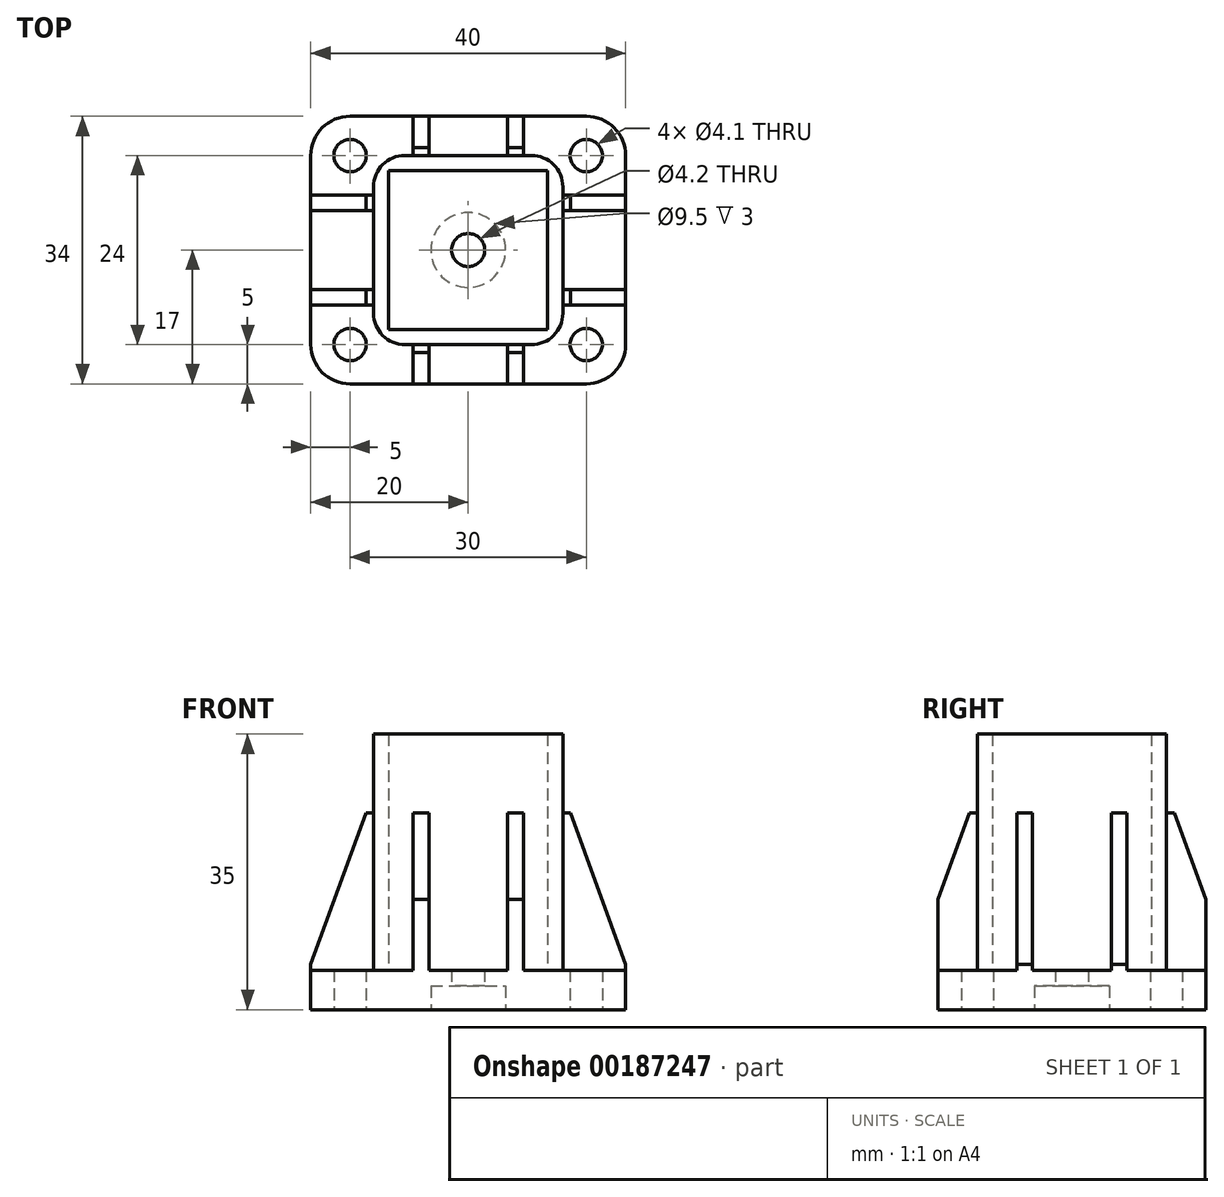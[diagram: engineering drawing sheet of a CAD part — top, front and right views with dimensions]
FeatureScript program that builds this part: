
annotation { "Feature Type Name" : "Feature", "Feature Type Description" : "" }
export const myFeature = defineFeature(function(context is Context, id is Id, definition is map)
    precondition{}
    {
        {
            var Q0;
            Q0=qCreatedBy(makeId("Top.planeOp"),FACE);
            var sketch = newSketch(context, id + "F0", { "sketchPlane" : qUnion([Q0])});
            skLineSegment(sketch, "E0.bottom", {"start": v(20, -17) * mm, "end": v(-20, -17) * mm});
            skLineSegment(sketch, "E0.top", {"start": v(20, 17) * mm, "end": v(-20, 17) * mm});
            skLineSegment(sketch, "E0.left", {"start": v(20, -17) * mm, "end": v(20, 17) * mm});
            skLineSegment(sketch, "E0.right", {"start": v(-20, -17) * mm, "end": v(-20, 17) * mm});
            skPoint(sketch, "E0.middle", {"position": v(0, 0) * mm});
            skCircle(sketch, "E1", {"center": v(0, 0) * mm, "radius": 2.1 * mm});
            skLineSegment(sketch, "E2", {"start": v(0, 0) * mm, "end": v(15, 0) * mm, "construction": true});
            skLineSegment(sketch, "E3", {"start": v(15, 0) * mm, "end": v(15, 12) * mm, "construction": true});
            skCircle(sketch, "E4", {"center": v(15, 12) * mm, "radius": 2.05 * mm});
            skLineSegment(sketch, "E5", {"start": v(0, 0) * mm, "end": v(0, 15.27) * mm, "construction": true});
            skLineSegment(sketch, "E6", {"start": v(0, 0) * mm, "end": v(0, -14.9) * mm, "construction": true});
            skCircle(sketch, "E7.MirrorC", {"center": v(15, -12) * mm, "radius": 2.05 * mm});
            skCircle(sketch, "E8.MirrorC", {"center": v(-15, 12) * mm, "radius": 2.05 * mm});
            skCircle(sketch, "E9.MirrorC", {"center": v(-15, -12) * mm, "radius": 2.05 * mm});
            skSolve(sketch);
        }
        {
            var Q0;
            Q0=makeQuery(id+"F0.imprint","IMPRINT",FACE,{"disambiguationData":[TD([[makeQuery(id+"F0.imprint","IMPRINT",EDGE,{"derivedFrom":sQuery(id+"F0.wireOp",EDGE,"E0.bottom")}),-1.0]])]});
            extrude(context, id + "F1", {"entities" : qUnion([Q0]), "depth" : 5 * mm});
        }
        {
            var Q0;
            Q0=makeQuery(id+"F1.opExtrude","CAP_FACE",FACE,{"disambiguationData":[OSD([sQuery(id+"F0.wireOp",EDGE,"E0.bottom"),sQuery(id+"F0.wireOp",EDGE,"E0.top"),sQuery(id+"F0.wireOp",EDGE,"E0.left"),sQuery(id+"F0.wireOp",EDGE,"E0.right"),sQuery(id+"F0.wireOp",EDGE,"E1"),sQuery(id+"F0.wireOp",EDGE,"E4"),sQuery(id+"F0.wireOp",EDGE,"E7.MirrorC"),sQuery(id+"F0.wireOp",EDGE,"E8.MirrorC"),sQuery(id+"F0.wireOp",EDGE,"E9.MirrorC")])],"isStart":true});
            var sketch = newSketch(context, id + "F2", { "sketchPlane" : qUnion([Q0])});
            skCircle(sketch, "E10", {"center": v(0, 0) * mm, "radius": 4.75 * mm});
            skSolve(sketch);
        }
        {
            var Q0;
            Q0=makeQuery(id+"F2.imprint","IMPRINT",FACE,{"disambiguationData":[TD([[makeQuery(id+"F2.imprint","IMPRINT",EDGE,{"derivedFrom":sQuery(id+"F2.wireOp",EDGE,"E10")}),1.0]])]});
            extrude(context, id + "F3", {"entities" : qUnion([Q0]), "operationType" : NewBodyOperationType.REMOVE, "oppositeDirection" : true, "depth" : 3 * mm});
        }
        {
            var Q0;
            Q0=makeQuery(id+"F1.opExtrude","CAP_FACE",FACE,{"disambiguationData":[OSD([sQuery(id+"F0.wireOp",EDGE,"E0.bottom"),sQuery(id+"F0.wireOp",EDGE,"E0.top"),sQuery(id+"F0.wireOp",EDGE,"E0.left"),sQuery(id+"F0.wireOp",EDGE,"E0.right"),sQuery(id+"F0.wireOp",EDGE,"E1"),sQuery(id+"F0.wireOp",EDGE,"E4"),sQuery(id+"F0.wireOp",EDGE,"E7.MirrorC"),sQuery(id+"F0.wireOp",EDGE,"E8.MirrorC"),sQuery(id+"F0.wireOp",EDGE,"E9.MirrorC")])],"isStart":false});
            var sketch = newSketch(context, id + "F4", { "sketchPlane" : qUnion([Q0])});
            skLineSegment(sketch, "E11.bottom", {"start": v(10.1, -10.1) * mm, "end": v(-10.1, -10.1) * mm});
            skLineSegment(sketch, "E11.top", {"start": v(10.1, 10.1) * mm, "end": v(-10.1, 10.1) * mm});
            skLineSegment(sketch, "E11.left", {"start": v(10.1, -10.1) * mm, "end": v(10.1, 10.1) * mm});
            skLineSegment(sketch, "E11.right", {"start": v(-10.1, -10.1) * mm, "end": v(-10.1, 10.1) * mm});
            skPoint(sketch, "E11.middle", {"position": v(0, 0) * mm});
            skLineSegment(sketch, "E12.bottom", {"start": v(12.03, -12.03) * mm, "end": v(-12.03, -12.03) * mm});
            skLineSegment(sketch, "E12.top", {"start": v(12.03, 12.03) * mm, "end": v(-12.03, 12.02) * mm});
            skLineSegment(sketch, "E12.left", {"start": v(12.03, -12.03) * mm, "end": v(12.03, 12.03) * mm});
            skLineSegment(sketch, "E12.right", {"start": v(-12.03, -12.03) * mm, "end": v(-12.03, 12.02) * mm});
            skLineSegment(sketch, "E13", {"start": v(0, 0) * mm, "end": v(0, 17) * mm, "construction": true});
            skLineSegment(sketch, "E14", {"start": v(0, 0) * mm, "end": v(20, 0) * mm, "construction": true});
            skPoint(sketch, "E15.end.orphan", {"position": v(1, 17) * mm});
            skPoint(sketch, "E15.start.orphan", {"position": v(1, 12.02) * mm});
            skPoint(sketch, "E16.MirrorCS.end.orphan", {"position": v(-1, 17) * mm});
            skPoint(sketch, "E16.MirrorCS.start.orphan", {"position": v(-1, 12.02) * mm});
            skPoint(sketch, "E17.MirrorCS.end.orphan", {"position": v(1, -17) * mm});
            skPoint(sketch, "E17.MirrorCS.start.orphan", {"position": v(1, -12.02) * mm});
            skPoint(sketch, "E18.MirrorCS.end.orphan", {"position": v(-1, -17) * mm});
            skPoint(sketch, "E18.MirrorCS.start.orphan", {"position": v(-1, -12.02) * mm});
            skPoint(sketch, "E19.end.orphan", {"position": v(7, 17) * mm});
            skPoint(sketch, "E19.start.orphan", {"position": v(7, 12.02) * mm});
            skPoint(sketch, "E20.end.orphan", {"position": v(5, 17) * mm});
            skPoint(sketch, "E20.start.orphan", {"position": v(5, 12.02) * mm});
            skPoint(sketch, "E21.MirrorCS.end.orphan", {"position": v(-5, 17) * mm});
            skPoint(sketch, "E21.MirrorCS.start.orphan", {"position": v(-5, 12.02) * mm});
            skPoint(sketch, "E22.MirrorCS.end.orphan", {"position": v(-7, 17) * mm});
            skPoint(sketch, "E22.MirrorCS.start.orphan", {"position": v(-7, 12.02) * mm});
            skPoint(sketch, "E23.end.orphan", {"position": v(20, 5) * mm});
            skPoint(sketch, "E23.start.orphan", {"position": v(12.03, 5) * mm});
            skPoint(sketch, "E24.end.orphan", {"position": v(20, 7) * mm});
            skPoint(sketch, "E24.start.orphan", {"position": v(12.03, 7) * mm});
            skPoint(sketch, "E25.MirrorCS.end.orphan", {"position": v(20, -5) * mm});
            skPoint(sketch, "E25.MirrorCS.start.orphan", {"position": v(12.03, -5) * mm});
            skPoint(sketch, "E26.MirrorCS.end.orphan", {"position": v(20, -7) * mm});
            skPoint(sketch, "E26.MirrorCS.start.orphan", {"position": v(12.03, -7) * mm});
            skPoint(sketch, "E27.MirrorCS.end.orphan", {"position": v(7, -17) * mm});
            skPoint(sketch, "E27.MirrorCS.start.orphan", {"position": v(7, -12.02) * mm});
            skPoint(sketch, "E28.MirrorCS.end.orphan", {"position": v(5, -17) * mm});
            skPoint(sketch, "E28.MirrorCS.start.orphan", {"position": v(5, -12.02) * mm});
            skPoint(sketch, "E29.MirrorCS.end.orphan", {"position": v(-5, -17) * mm});
            skPoint(sketch, "E29.MirrorCS.start.orphan", {"position": v(-5, -12.02) * mm});
            skPoint(sketch, "E30.MirrorCS.end.orphan", {"position": v(-20, 5) * mm});
            skPoint(sketch, "E30.MirrorCS.start.orphan", {"position": v(-12.03, 5) * mm});
            skPoint(sketch, "E31.MirrorCS.end.orphan", {"position": v(-20, 7) * mm});
            skPoint(sketch, "E31.MirrorCS.start.orphan", {"position": v(-12.03, 7) * mm});
            skPoint(sketch, "E32.MirrorCS.end.orphan", {"position": v(-20, -7) * mm});
            skPoint(sketch, "E32.MirrorCS.start.orphan", {"position": v(-12.03, -7) * mm});
            skPoint(sketch, "E33.MirrorCS.end.orphan", {"position": v(-20, -5) * mm});
            skPoint(sketch, "E33.MirrorCS.start.orphan", {"position": v(-12.03, -5) * mm});
            skPoint(sketch, "E34.MirrorCS.end.orphan", {"position": v(-7, -17) * mm});
            skPoint(sketch, "E34.MirrorCS.start.orphan", {"position": v(-7, -12.02) * mm});
            skSolve(sketch);
        }
        {
            var Q0;
            Q0=makeQuery(id+"F4.imprint","IMPRINT",FACE,{"disambiguationData":[TD([[makeQuery(id+"F4.imprint","IMPRINT",EDGE,{"derivedFrom":sQuery(id+"F4.wireOp",EDGE,"E11.bottom")}),1.0]])]});
            extrude(context, id + "F5", {"entities" : qUnion([Q0]), "operationType" : NewBodyOperationType.ADD, "depth" : 30 * mm});
        }
        {
            var Q0;
            Q0=makeQuery(id+"F1.opExtrude","SWEPT_EDGE",EDGE,{"disambiguationData":[OSD([sQuery(id+"F0.wireOp",EDGE,"E0.top"),sQuery(id+"F0.wireOp",EDGE,"E0.left")])]});
            var Q1;
            Q1=makeQuery(id+"F1.opExtrude","SWEPT_EDGE",EDGE,{"disambiguationData":[OSD([sQuery(id+"F0.wireOp",EDGE,"E0.bottom"),sQuery(id+"F0.wireOp",EDGE,"E0.left")])]});
            var Q2;
            Q2=makeQuery(id+"F1.opExtrude","SWEPT_EDGE",EDGE,{"disambiguationData":[OSD([sQuery(id+"F0.wireOp",EDGE,"E0.bottom"),sQuery(id+"F0.wireOp",EDGE,"E0.right")])]});
            var Q3;
            Q3=makeQuery(id+"F1.opExtrude","SWEPT_EDGE",EDGE,{"disambiguationData":[OSD([sQuery(id+"F0.wireOp",EDGE,"E0.top"),sQuery(id+"F0.wireOp",EDGE,"E0.right")])]});
            fillet(context, id + "F6", {"entities" : qUnion([Q0, Q1, Q2, Q3]), "radius" : 5 * mm, "tangentPropagation" : true, "allowEdgeOverflow" : false});
        }
        {
            var Q0;
            Q0=makeQuery(id+"F5.opExtrude","SWEPT_EDGE",EDGE,{"disambiguationData":[OSD([sQuery(id+"F4.wireOp",EDGE,"E12.bottom"),sQuery(id+"F4.wireOp",EDGE,"E12.left")])]});
            var Q1;
            Q1=makeQuery(id+"F5.opExtrude","SWEPT_EDGE",EDGE,{"disambiguationData":[OSD([sQuery(id+"F4.wireOp",EDGE,"E12.top"),sQuery(id+"F4.wireOp",EDGE,"E12.left")])]});
            var Q2;
            Q2=makeQuery(id+"F5.opExtrude","SWEPT_EDGE",EDGE,{"disambiguationData":[OSD([sQuery(id+"F4.wireOp",EDGE,"E12.bottom"),sQuery(id+"F4.wireOp",EDGE,"E12.right")])]});
            var Q3;
            Q3=makeQuery(id+"F5.opExtrude","SWEPT_EDGE",EDGE,{"disambiguationData":[OSD([sQuery(id+"F4.wireOp",EDGE,"E12.top"),sQuery(id+"F4.wireOp",EDGE,"E12.right")])]});
            fillet(context, id + "F7", {"entities" : qUnion([Q0, Q1, Q2, Q3]), "radius" : 4 * mm, "tangentPropagation" : true, "allowEdgeOverflow" : false});
        }
        {
            var Q0;
            {var subQ0=sQuery(id+"F0.wireOp",EDGE,"E8.MirrorC");var subQ1=sQuery(id+"F0.wireOp",EDGE,"E7.MirrorC");var subQ2=sQuery(id+"F0.wireOp",EDGE,"E4");var subQ3=sQuery(id+"F0.wireOp",EDGE,"E0.bottom");var subQ4=sQuery(id+"F0.wireOp",EDGE,"E9.MirrorC");var subQ5=sQuery(id+"F0.wireOp",EDGE,"E0.top");var subQ6=sQuery(id+"F0.wireOp",EDGE,"E0.left");var subQ7=sQuery(id+"F0.wireOp",EDGE,"E0.right");Q0=makeQuery(id+"F5.boolean.opBoolean","SPLIT",FACE,{"disambiguationData":[TD([makeQuery(id+"F1.opExtrude","SWEPT_FACE",FACE,{"disambiguationData":[OSD([subQ3])]})])],"derivedFrom":makeQuery(id+"F1.opExtrude","CAP_FACE",FACE,{"disambiguationData":[OSD([subQ3,subQ5,subQ6,subQ7,sQuery(id+"F0.wireOp",EDGE,"E1"),subQ2,subQ1,subQ0,subQ4])],"isStart":false})});}
            var sketch = newSketch(context, id + "F8", { "sketchPlane" : qUnion([Q0])});
            skLineSegment(sketch, "E35", {"start": v(0, 0) * mm, "end": v(0, 17) * mm, "construction": true});
            skLineSegment(sketch, "E36", {"start": v(0, 0) * mm, "end": v(20, 0) * mm, "construction": true});
            skLineSegment(sketch, "E37", {"start": v(5, 12.03) * mm, "end": v(5, 17) * mm});
            skLineSegment(sketch, "E38", {"start": v(7, 12.03) * mm, "end": v(7, 17) * mm});
            skLineSegment(sketch, "E39", {"start": v(12.03, 7) * mm, "end": v(20, 7) * mm});
            skLineSegment(sketch, "E40", {"start": v(12.03, 5) * mm, "end": v(20, 5) * mm});
            skLineSegment(sketch, "E41.MirrorCS", {"start": v(-5, 12.03) * mm, "end": v(-5, 17) * mm});
            skLineSegment(sketch, "E42.MirrorCS", {"start": v(-7, 12.03) * mm, "end": v(-7, 17) * mm});
            skLineSegment(sketch, "E43.MirrorCS", {"start": v(12.03, -5) * mm, "end": v(20, -5) * mm});
            skLineSegment(sketch, "E44.MirrorCS", {"start": v(12.03, -7) * mm, "end": v(20, -7) * mm});
            skLineSegment(sketch, "E45.MirrorCS", {"start": v(-12.03, 7) * mm, "end": v(-20, 7) * mm});
            skLineSegment(sketch, "E46.MirrorCS", {"start": v(-12.03, 5) * mm, "end": v(-20, 5) * mm});
            skLineSegment(sketch, "E47.MirrorCS", {"start": v(-12.03, -5) * mm, "end": v(-20, -5) * mm});
            skLineSegment(sketch, "E48.MirrorCS", {"start": v(-12.03, -7) * mm, "end": v(-20, -7) * mm});
            skLineSegment(sketch, "E49.MirrorCS", {"start": v(7, -12.03) * mm, "end": v(7, -17) * mm});
            skLineSegment(sketch, "E50.MirrorCS", {"start": v(5, -12.03) * mm, "end": v(5, -17) * mm});
            skLineSegment(sketch, "E51.MirrorCS", {"start": v(-5, -12.03) * mm, "end": v(-5, -17) * mm});
            skLineSegment(sketch, "E52.MirrorCS", {"start": v(-7, -12.03) * mm, "end": v(-7, -17) * mm});
            skSolve(sketch);
        }
        {
            var Q0;
            {var subQ0=sQuery(id+"F8.wireOp",EDGE,"E41.MirrorCS");Q0=makeQuery(id+"F8.imprint","IMPRINT",FACE,{"disambiguationData":[TD([[makeQuery(id+"F8.imprint","IMPRINT",EDGE,{"derivedFrom":subQ0}),1.0]])]});}
            var Q1;
            {var subQ0=sQuery(id+"F8.wireOp",EDGE,"E37");Q1=makeQuery(id+"F8.imprint","IMPRINT",FACE,{"disambiguationData":[TD([[makeQuery(id+"F8.imprint","IMPRINT",EDGE,{"derivedFrom":subQ0}),-1.0]])]});}
            var Q2;
            {var subQ0=sQuery(id+"F8.wireOp",EDGE,"E39");Q2=makeQuery(id+"F8.imprint","IMPRINT",FACE,{"disambiguationData":[TD([[makeQuery(id+"F8.imprint","IMPRINT",EDGE,{"derivedFrom":subQ0}),-1.0]])]});}
            var Q3;
            {var subQ0=sQuery(id+"F8.wireOp",EDGE,"E43.MirrorCS");Q3=makeQuery(id+"F8.imprint","IMPRINT",FACE,{"disambiguationData":[TD([[makeQuery(id+"F8.imprint","IMPRINT",EDGE,{"derivedFrom":subQ0}),-1.0]])]});}
            var Q4;
            {var subQ0=sQuery(id+"F8.wireOp",EDGE,"E49.MirrorCS");Q4=makeQuery(id+"F8.imprint","IMPRINT",FACE,{"disambiguationData":[TD([[makeQuery(id+"F8.imprint","IMPRINT",EDGE,{"derivedFrom":subQ0}),-1.0]])]});}
            var Q5;
            {var subQ0=sQuery(id+"F8.wireOp",EDGE,"E51.MirrorCS");Q5=makeQuery(id+"F8.imprint","IMPRINT",FACE,{"disambiguationData":[TD([[makeQuery(id+"F8.imprint","IMPRINT",EDGE,{"derivedFrom":subQ0}),-1.0]])]});}
            var Q6;
            {var subQ0=sQuery(id+"F8.wireOp",EDGE,"E47.MirrorCS");Q6=makeQuery(id+"F8.imprint","IMPRINT",FACE,{"disambiguationData":[TD([[makeQuery(id+"F8.imprint","IMPRINT",EDGE,{"derivedFrom":subQ0}),1.0]])]});}
            var Q7;
            {var subQ0=sQuery(id+"F8.wireOp",EDGE,"E45.MirrorCS");Q7=makeQuery(id+"F8.imprint","IMPRINT",FACE,{"disambiguationData":[TD([[makeQuery(id+"F8.imprint","IMPRINT",EDGE,{"derivedFrom":subQ0}),1.0]])]});}
            extrude(context, id + "F9", {"entities" : qUnion([Q0, Q1, Q2, Q3, Q4, Q5, Q6, Q7]), "operationType" : NewBodyOperationType.ADD, "depth" : 20 * mm});
        }
        {
            var Q0;
            {var subQ0=sQuery(id+"F0.wireOp",EDGE,"E0.left");var subQ1=makeQuery(id+"F1.opExtrude","CAP_EDGE",EDGE,{"disambiguationData":[OSD([subQ0])],"isStart":false});Q0=makeQuery(id+"F9.opExtrude","CAP_EDGE",EDGE,{"disambiguationData":[OSD([subQ0]),TDD([makeQuery(id+"F8.imprint","IMPRINT",EDGE,{"disambiguationData":[TD([[makeQuery(id+"F8.imprint","INTERSECT",VERTEX,{"derivedFrom":[subQ1,sQuery(id+"F8.wireOp",EDGE,"E39")]}),1.0]])],"derivedFrom":subQ1})])],"isStart":false});}
            var Q1;
            {var subQ0=sQuery(id+"F0.wireOp",EDGE,"E0.left");var subQ1=makeQuery(id+"F1.opExtrude","CAP_EDGE",EDGE,{"disambiguationData":[OSD([subQ0])],"isStart":false});Q1=makeQuery(id+"F9.opExtrude","CAP_EDGE",EDGE,{"disambiguationData":[OSD([subQ0]),TDD([makeQuery(id+"F8.imprint","IMPRINT",EDGE,{"disambiguationData":[TD([[makeQuery(id+"F8.imprint","INTERSECT",VERTEX,{"derivedFrom":[subQ1,sQuery(id+"F8.wireOp",EDGE,"E43.MirrorCS")]}),1.0]])],"derivedFrom":subQ1})])],"isStart":false});}
            chamfer(context, id + "F10", {"entities" : qUnion([Q0, Q1]), "chamferType" : ChamferType.OFFSET_ANGLE, "width" : 7 * mm, "oppositeDirection" : false, "angle" : 70 * degree, "tangentPropagation" : true});
        }
        {
            var Q0;
            {var subQ0=sQuery(id+"F0.wireOp",EDGE,"E0.right");var subQ1=makeQuery(id+"F1.opExtrude","CAP_EDGE",EDGE,{"disambiguationData":[OSD([subQ0])],"isStart":false});Q0=makeQuery(id+"F9.opExtrude","CAP_EDGE",EDGE,{"disambiguationData":[OSD([subQ0]),TDD([makeQuery(id+"F8.imprint","IMPRINT",EDGE,{"disambiguationData":[TD([[makeQuery(id+"F8.imprint","INTERSECT",VERTEX,{"derivedFrom":[subQ1,sQuery(id+"F8.wireOp",EDGE,"E45.MirrorCS")]}),1.0]])],"derivedFrom":subQ1})])],"isStart":false});}
            var Q1;
            {var subQ0=sQuery(id+"F0.wireOp",EDGE,"E0.right");var subQ1=makeQuery(id+"F1.opExtrude","CAP_EDGE",EDGE,{"disambiguationData":[OSD([subQ0])],"isStart":false});Q1=makeQuery(id+"F9.opExtrude","CAP_EDGE",EDGE,{"disambiguationData":[OSD([subQ0]),TDD([makeQuery(id+"F8.imprint","IMPRINT",EDGE,{"disambiguationData":[TD([[makeQuery(id+"F8.imprint","INTERSECT",VERTEX,{"derivedFrom":[subQ1,sQuery(id+"F8.wireOp",EDGE,"E47.MirrorCS")]}),1.0]])],"derivedFrom":subQ1})])],"isStart":false});}
            chamfer(context, id + "F11", {"entities" : qUnion([Q0, Q1]), "chamferType" : ChamferType.OFFSET_ANGLE, "width" : 7 * mm, "oppositeDirection" : true, "angle" : 70 * degree, "tangentPropagation" : true});
        }
        {
            var Q0;
            {var subQ0=sQuery(id+"F0.wireOp",EDGE,"E0.bottom");var subQ1=makeQuery(id+"F1.opExtrude","CAP_EDGE",EDGE,{"disambiguationData":[OSD([subQ0])],"isStart":false});Q0=makeQuery(id+"F9.opExtrude","CAP_EDGE",EDGE,{"disambiguationData":[OSD([subQ0]),TDD([makeQuery(id+"F8.imprint","IMPRINT",EDGE,{"disambiguationData":[TD([[makeQuery(id+"F8.imprint","INTERSECT",VERTEX,{"derivedFrom":[subQ1,sQuery(id+"F8.wireOp",EDGE,"E49.MirrorCS")]}),-1.0]])],"derivedFrom":subQ1})])],"isStart":false});}
            var Q1;
            {var subQ0=sQuery(id+"F0.wireOp",EDGE,"E0.bottom");var subQ1=makeQuery(id+"F1.opExtrude","CAP_EDGE",EDGE,{"disambiguationData":[OSD([subQ0])],"isStart":false});Q1=makeQuery(id+"F9.opExtrude","CAP_EDGE",EDGE,{"disambiguationData":[OSD([subQ0]),TDD([makeQuery(id+"F8.imprint","IMPRINT",EDGE,{"disambiguationData":[TD([[makeQuery(id+"F8.imprint","INTERSECT",VERTEX,{"derivedFrom":[subQ1,sQuery(id+"F8.wireOp",EDGE,"E51.MirrorCS")]}),-1.0]])],"derivedFrom":subQ1})])],"isStart":false});}
            chamfer(context, id + "F12", {"entities" : qUnion([Q0, Q1]), "chamferType" : ChamferType.OFFSET_ANGLE, "width" : 4 * mm, "oppositeDirection" : true, "angle" : 70 * degree, "tangentPropagation" : true});
        }
        {
            var Q0;
            {var subQ0=sQuery(id+"F0.wireOp",EDGE,"E0.top");var subQ1=makeQuery(id+"F1.opExtrude","CAP_EDGE",EDGE,{"disambiguationData":[OSD([subQ0])],"isStart":false});Q0=makeQuery(id+"F9.opExtrude","CAP_EDGE",EDGE,{"disambiguationData":[OSD([subQ0]),TDD([makeQuery(id+"F8.imprint","IMPRINT",EDGE,{"disambiguationData":[TD([[makeQuery(id+"F8.imprint","INTERSECT",VERTEX,{"derivedFrom":[subQ1,sQuery(id+"F8.wireOp",EDGE,"E41.MirrorCS")]}),-1.0]])],"derivedFrom":subQ1})])],"isStart":false});}
            var Q1;
            {var subQ0=sQuery(id+"F0.wireOp",EDGE,"E0.top");var subQ1=makeQuery(id+"F1.opExtrude","CAP_EDGE",EDGE,{"disambiguationData":[OSD([subQ0])],"isStart":false});Q1=makeQuery(id+"F9.opExtrude","CAP_EDGE",EDGE,{"disambiguationData":[OSD([subQ0]),TDD([makeQuery(id+"F8.imprint","IMPRINT",EDGE,{"disambiguationData":[TD([[makeQuery(id+"F8.imprint","INTERSECT",VERTEX,{"derivedFrom":[subQ1,sQuery(id+"F8.wireOp",EDGE,"E37")]}),1.0]])],"derivedFrom":subQ1})])],"isStart":false});}
            chamfer(context, id + "F13", {"entities" : qUnion([Q0, Q1]), "chamferType" : ChamferType.OFFSET_ANGLE, "width" : 4 * mm, "oppositeDirection" : false, "angle" : 70 * degree, "tangentPropagation" : true});
        }
    });
